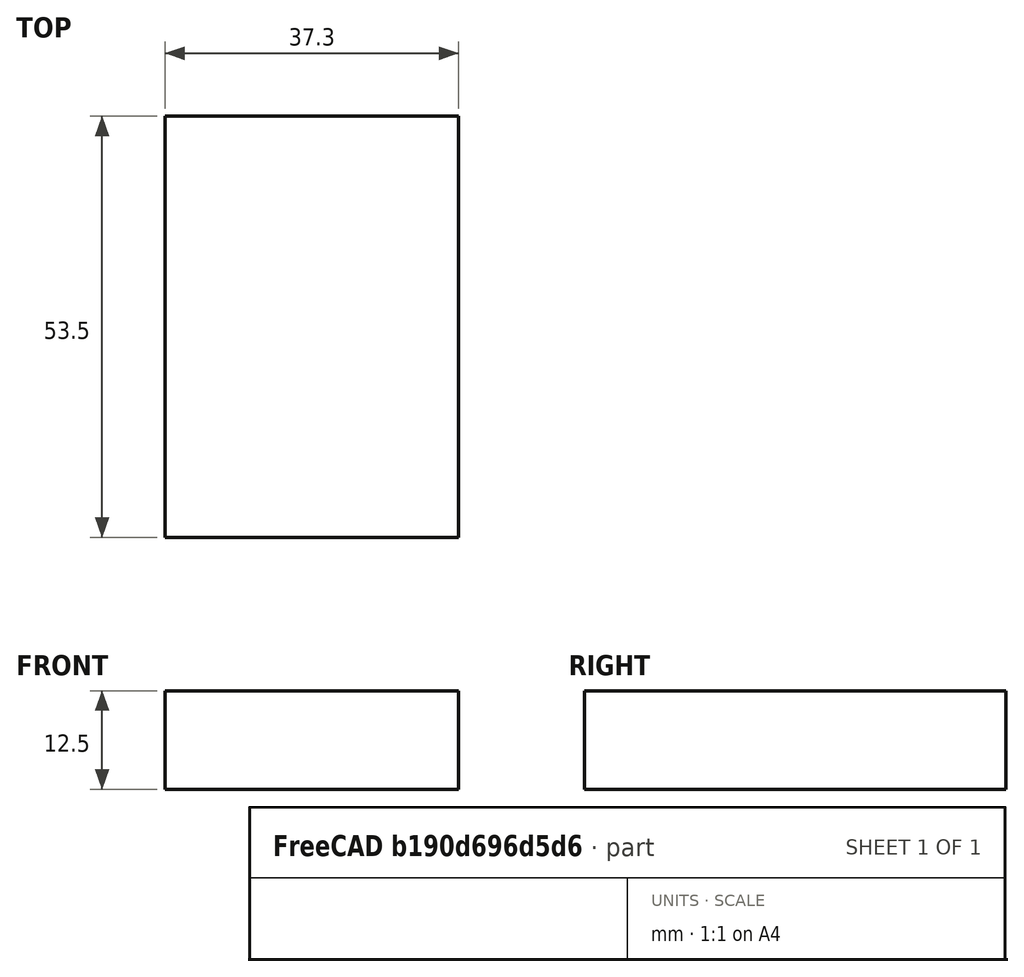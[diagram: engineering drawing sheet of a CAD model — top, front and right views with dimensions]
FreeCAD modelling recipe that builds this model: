
FCSTD DOCUMENT  (FreeCAD 0.20R29410 (Git))
Label: battery
License: All rights reserved
LicenseURL: http://en.wikipedia.org/wiki/All_rights_reserved
objects: Sketcher::SketchObject×1, PartDesign::Pad×1, PartDesign::Body×1, App::Link×1
note: 4 computed .brp shape members not serialized (recipe doc carries the construction recipe); baked Part::Feature solids carry a one-line shape summary decoded from their .brp

FEATURE [Sketcher::SketchObject] Sketch
  FullyConstrained = true
  MapMode = 5
  Support = -> [XY_Plane]
  sketch-geometry (4):
    g0: LineSegment StartX=-18.65 StartY=26.75 StartZ=0 EndX=18.65 EndY=26.75 EndZ=0
    g1: LineSegment StartX=18.65 StartY=26.75 StartZ=0 EndX=18.65 EndY=-26.75 EndZ=0
    g2: LineSegment StartX=18.65 StartY=-26.75 StartZ=0 EndX=-18.65 EndY=-26.75 EndZ=0
    g3: LineSegment StartX=-18.65 StartY=-26.75 StartZ=0 EndX=-18.65 EndY=26.75 EndZ=0
  constraints (10):
    c: Coincident(g0,g1)
    c: Coincident(g1,g2)
    c: Coincident(g2,g3)
    c: Coincident(g3,g0)
    c: Horizontal(g2)
    c: Vertical(g1)
    c: DistanceY(g1,g1) = 53.5
    c: DistanceX(g0,g0) = 37.3
    c: Symmetric(g0,g0,g-2)
    c: Symmetric(g2,g0,g-1)
FEATURE [PartDesign::Pad] Pad  label="pad"
  Direction = (0,0,1)
  Length = 12.5
  Length2 = 10
  Profile = -> Sketch
  ReferenceAxis = -> Sketch [N_Axis]
  Type = 0
FEATURE [PartDesign::Body] Body  label="battery"
  Group = -> [Sketch,Pad]
  Origin = -> Origin
  Tip = -> Pad
FEATURE [App::Link] Link  label="battery001"
  LinkedObject = -> Body
